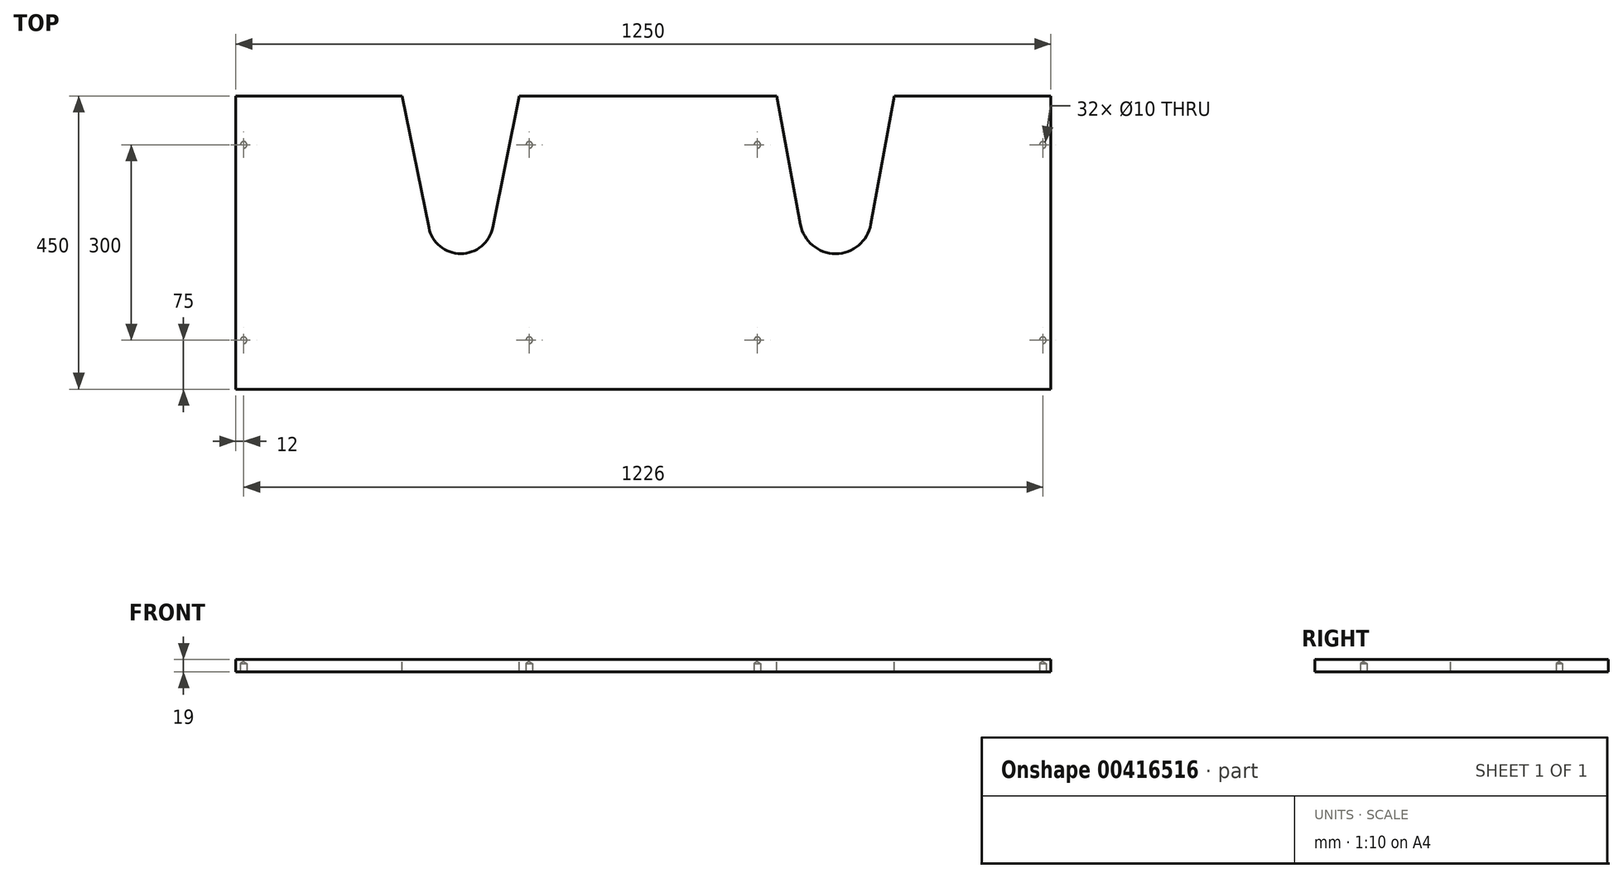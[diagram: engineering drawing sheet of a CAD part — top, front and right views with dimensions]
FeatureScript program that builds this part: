
annotation { "Feature Type Name" : "Feature", "Feature Type Description" : "" }
export const myFeature = defineFeature(function(context is Context, id is Id, definition is map)
    precondition{}
    {
        {
            var Q0;
            Q0=qCreatedBy(makeId("Top.planeOp"),FACE);
            var sketch = newSketch(context, id + "F0", { "sketchPlane" : qUnion([Q0])});
            skLineSegment(sketch, "E0.bottom", {"start": v(-625, 225) * mm, "end": v(625, 225) * mm});
            skLineSegment(sketch, "E0.top", {"start": v(-625, -225) * mm, "end": v(625, -225) * mm});
            skLineSegment(sketch, "E0.left", {"start": v(-625, 225) * mm, "end": v(-625, -225) * mm});
            skLineSegment(sketch, "E0.right", {"start": v(625, 225) * mm, "end": v(625, -225) * mm});
            skPoint(sketch, "E0.middle", {"position": v(0, 0) * mm});
            skSolve(sketch);
        }
        {
            var Q0;
            Q0=makeQuery(id+"F0.imprint","IMPRINT",FACE,{"disambiguationData":[TD([[makeQuery(id+"F0.imprint","IMPRINT",EDGE,{"derivedFrom":sQuery(id+"F0.wireOp",EDGE,"E0.bottom")}),-1.0]])]});
            extrude(context, id + "F1", {"entities" : qUnion([Q0]), "depth" : 19 * mm});
        }
        {
            var Q0;
            Q0=makeQuery(id+"F1.opExtrude","CAP_FACE",FACE,{"disambiguationData":[OSD([sQuery(id+"F0.wireOp",EDGE,"E0.bottom"),sQuery(id+"F0.wireOp",EDGE,"E0.top"),sQuery(id+"F0.wireOp",EDGE,"E0.left"),sQuery(id+"F0.wireOp",EDGE,"E0.right")])],"isStart":false});
            var sketch = newSketch(context, id + "F2", { "sketchPlane" : qUnion([Q0])});
            skLineSegment(sketch, "E1", {"start": v(-280, 225) * mm, "end": v(-280, -159) * mm, "construction": true});
            skLineSegment(sketch, "E2", {"start": v(-369.44, 33) * mm, "end": v(-205.4, 33) * mm, "construction": true});
            skLineSegment(sketch, "E3", {"start": v(-370, 225) * mm, "end": v(-190, 225) * mm});
            skLineSegment(sketch, "E4", {"start": v(-190, 225) * mm, "end": v(-231, 23.05) * mm});
            skLineSegment(sketch, "E5", {"start": v(-370, 225) * mm, "end": v(-329, 23.05) * mm});
            skArc(sketch, "E6", {"start": v(-329, 23.05) * mm, "mid": v(-280, -17) * mm, "end": v(-231, 23.05) * mm});
            skSolve(sketch);
        }
        {
            var Q0;
            Q0=makeQuery(id+"F2.imprint","IMPRINT",FACE,{"disambiguationData":[TD([[makeQuery(id+"F2.imprint","IMPRINT",EDGE,{"derivedFrom":sQuery(id+"F2.wireOp",EDGE,"E3")}),-1.0]])]});
            extrude(context, id + "F3", {"entities" : qUnion([Q0]), "operationType" : NewBodyOperationType.REMOVE, "endBound" : BoundingType.UP_TO_NEXT, "oppositeDirection" : true, "depth" : 25 * mm});
        }
        {
            var Q0;
            Q0=makeQuery(id+"F1.opExtrude","CAP_FACE",FACE,{"disambiguationData":[OSD([sQuery(id+"F0.wireOp",EDGE,"E0.bottom"),sQuery(id+"F0.wireOp",EDGE,"E0.top"),sQuery(id+"F0.wireOp",EDGE,"E0.left"),sQuery(id+"F0.wireOp",EDGE,"E0.right")])],"isStart":false});
            var sketch = newSketch(context, id + "F4", { "sketchPlane" : qUnion([Q0])});
            skLineSegment(sketch, "E7", {"start": v(295, 248.09) * mm, "end": v(295, -70.96) * mm, "construction": true});
            skLineSegment(sketch, "E8", {"start": v(205, 225) * mm, "end": v(240.9, 28.14) * mm});
            skLineSegment(sketch, "E9", {"start": v(349.1, 28.14) * mm, "end": v(385, 225) * mm});
            skLineSegment(sketch, "E10", {"start": v(385, 225) * mm, "end": v(205, 225) * mm});
            skArc(sketch, "E11", {"start": v(240.9, 28.14) * mm, "mid": v(295, -17) * mm, "end": v(349.1, 28.14) * mm});
            skSolve(sketch);
        }
        {
            var Q0;
            Q0 = qSketchRegion(id + "F4", true);
            extrude(context, id + "F5", {"entities" : qUnion([Q0]), "operationType" : NewBodyOperationType.REMOVE, "endBound" : BoundingType.UP_TO_NEXT, "oppositeDirection" : true, "depth" : 25 * mm});
        }
        {
            var Q0;
            Q0=makeQuery(id+"F1.opExtrude","CAP_FACE",FACE,{"disambiguationData":[OSD([sQuery(id+"F0.wireOp",EDGE,"E0.bottom"),sQuery(id+"F0.wireOp",EDGE,"E0.top"),sQuery(id+"F0.wireOp",EDGE,"E0.left"),sQuery(id+"F0.wireOp",EDGE,"E0.right")])],"isStart":true});
            var sketch = newSketch(context, id + "F6", { "sketchPlane" : qUnion([Q0])});
            skPoint(sketch, "E12", {"position": v(-613, 150) * mm});
            skLineSegment(sketch, "E13", {"start": v(-694.12, 150) * mm, "end": v(667.4, 150) * mm, "construction": true});
            skPoint(sketch, "E14", {"position": v(-175, 150) * mm});
            skPoint(sketch, "E15", {"position": v(175, 150) * mm});
            skPoint(sketch, "E16", {"position": v(613, 150) * mm});
            skLineSegment(sketch, "E17", {"start": v(-674.95, -150) * mm, "end": v(658.23, -150) * mm, "construction": true});
            skPoint(sketch, "E18", {"position": v(-613, -150) * mm});
            skPoint(sketch, "E19", {"position": v(-175, -150) * mm});
            skPoint(sketch, "E20", {"position": v(175, -150) * mm});
            skPoint(sketch, "E21", {"position": v(613, -150) * mm});
            skSolve(sketch);
        }
        {
            var Q0;
            Q0=sQuery(id+"F6.wireOp",VERTEX,"E12");
            var Q1;
            Q1=sQuery(id+"F6.wireOp",VERTEX,"E14");
            var Q2;
            Q2=sQuery(id+"F6.wireOp",VERTEX,"E15");
            var Q3;
            Q3=sQuery(id+"F6.wireOp",VERTEX,"E16");
            var Q4;
            Q4=sQuery(id+"F6.wireOp",VERTEX,"E18");
            var Q5;
            Q5=sQuery(id+"F6.wireOp",VERTEX,"E19");
            var Q6;
            Q6=sQuery(id+"F6.wireOp",VERTEX,"E20");
            var Q7;
            Q7=sQuery(id+"F6.wireOp",VERTEX,"E21");
            var Q8;
            Q8=makeQuery(id+"F1.opExtrude","SWEPT_BODY",BODY,{"disambiguationData":[OSD([sQuery(id+"F0.wireOp",EDGE,"E0.bottom"),sQuery(id+"F0.wireOp",EDGE,"E0.top"),sQuery(id+"F0.wireOp",EDGE,"E0.left"),sQuery(id+"F0.wireOp",EDGE,"E0.right")])]});
            hole(context, id + "F7", {"style" : HoleStyle.SIMPLE, "endStyle" : HoleEndStyle.BLIND, "holeDiameter" : 10 * mm, "holeDepth" : 13 * mm, "isTappedThrough" : true, "tappedDepth" : 12 * mm, "tapClearance" : 3, "startFromSketch" : true, "locations" : qUnion([Q0, Q1, Q2, Q3, Q4, Q5, Q6, Q7]), "scope" : qUnion([Q8])});
        }
    });
